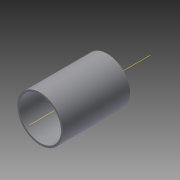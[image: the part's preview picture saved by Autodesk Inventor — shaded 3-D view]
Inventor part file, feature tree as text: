
AUTODESK INVENTOR PART (.ipt)
format: ipt  version: 2013 (Build 170138000, 138)  size: 82,944 bytes
history: native  units: mm
features: other x2, extrude x2, sketch x2
ambient origin geometry x8: Origin, YZ Plane, XZ Plane, XY Plane, X Axis, Y Axis, Z Axis, Center Point
feature tree (6):
  other  "ソリッド1"
  extrude  "押し出し1"  Depth=70.0mm
  extrude  "押し出し2"  Depth=64.0mm
  other  "作業軸1"
  sketch  "スケッチ1"
  sketch  "スケッチ2"
